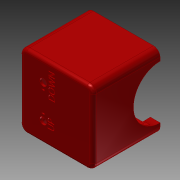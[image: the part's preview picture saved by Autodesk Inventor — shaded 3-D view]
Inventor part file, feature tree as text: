
AUTODESK INVENTOR PART (.ipt)
format: ipt  version: 2015 (Build 190159000, 159)  size: 363,008 bytes
history: native  units: in
note: dims shown in document units (in); Inventor stores cm internally (conversion verified against a paired STEP export)
features: extrude x5, sketch x5, shell x1, fillet x1
ambient origin geometry x8: Origin, YZ Plane, XZ Plane, XY Plane, X Axis, Y Axis, Z Axis, Center Point
bodies: Solid1 (feature_tree)
feature tree (12):
  extrude  "Extrusion1"  Depth=2.75in
  shell  "Shell1"  Thickness=0.25in
  extrude  "Extrusion2"  Depth=0.17in
  fillet  "Fillet2"  Radius=0.17in
  extrude  "Extrusion3"  Depth=1.0in TaperAngle=0.0deg
  extrude  "Extrusion4"  Depth=0.125in
  extrude  "Extrusion5"  Depth=1.0in
  sketch  "Sketch1"  dims[d0=2.75in d1=2.75in d2=0.25in]
  sketch  "Sketch4"  dims[d3=2.5in d4=0.0in d5=0.08in d7=0.17in]
  sketch  "Sketch5"  dims[d8=0.17in d9=1.0in d10=0.0in]
  sketch  "Sketch6"  dims[d11=0.1142in d12=0.125in]
  sketch  "Sketch7"  dims[d31=0.24in d32=0.27in d33=0.1in d34=0.05in d35=1.25in d36=0.5in d37=1.0in d38=0.0in d39=0.125in d40=0.125in d41=0.2033in d42=0.4975in d43=0.05in d44=0.0in d45=1.0in d46=1.0in d47=0.0in]
